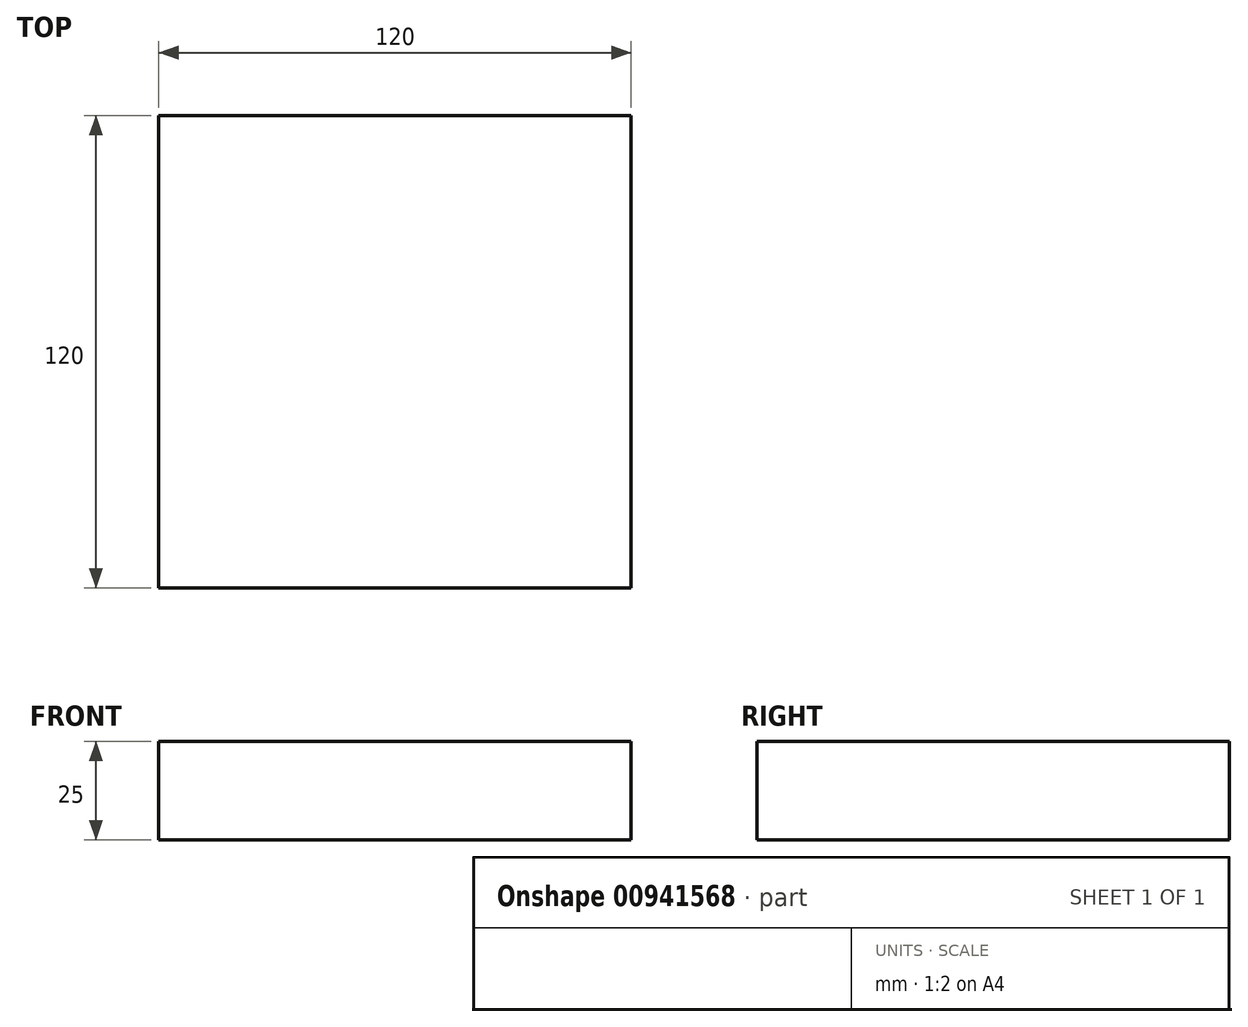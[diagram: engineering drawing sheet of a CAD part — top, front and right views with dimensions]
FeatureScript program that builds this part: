
annotation { "Feature Type Name" : "Feature", "Feature Type Description" : "" }
export const myFeature = defineFeature(function(context is Context, id is Id, definition is map)
    precondition{}
    {
        {
            var Q0;
            Q0=qCreatedBy(makeId("Top.planeOp"),FACE);
            var sketch = newSketch(context, id + "F0", { "sketchPlane" : qUnion([Q0])});
            skLineSegment(sketch, "E0.bottom", {"start": v(-55.54, 70.07) * mm, "end": v(64.46, 70.07) * mm});
            skLineSegment(sketch, "E0.top", {"start": v(-55.54, -49.93) * mm, "end": v(64.46, -49.93) * mm});
            skLineSegment(sketch, "E0.left", {"start": v(-55.54, 70.07) * mm, "end": v(-55.54, -49.93) * mm});
            skLineSegment(sketch, "E0.right", {"start": v(64.46, 70.07) * mm, "end": v(64.46, -49.93) * mm});
            skSolve(sketch);
        }
        {
            var Q0;
            Q0 = qSketchRegion(id + "F0", true);
            extrude(context, id + "F1", {"entities" : qUnion([Q0]), "depth" : 25 * mm, "offsetDistance" : 25 * mm});
        }
    });
